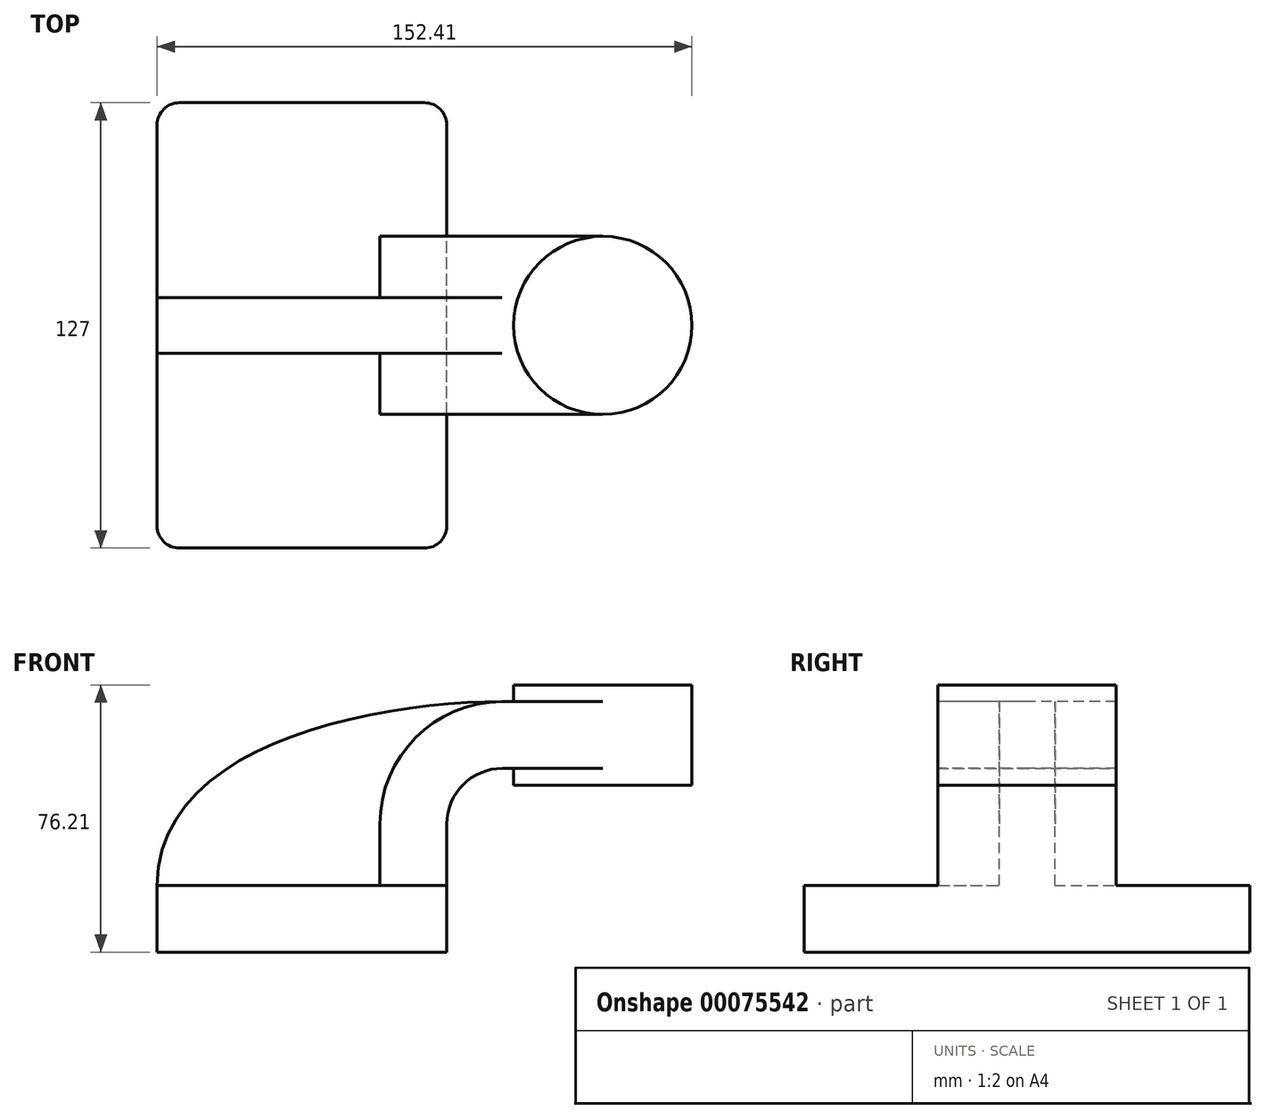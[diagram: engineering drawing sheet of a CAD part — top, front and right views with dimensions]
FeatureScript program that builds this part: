
annotation { "Feature Type Name" : "Feature", "Feature Type Description" : "" }
export const myFeature = defineFeature(function(context is Context, id is Id, definition is map)
    precondition{}
    {
        {
            var Q0;
            Q0=qCreatedBy(makeId("Front.planeOp"),FACE);
            var sketch = newSketch(context, id + "F0", { "sketchPlane" : qUnion([Q0])});
            skLineSegment(sketch, "E0.rect.bottom", {"start": v(-41.28, 9.53) * mm, "end": v(41.27, 9.53) * mm});
            skLineSegment(sketch, "E0.rect.top", {"start": v(-41.28, -9.53) * mm, "end": v(41.27, -9.53) * mm});
            skLineSegment(sketch, "E0.rect.left", {"start": v(-41.28, 9.53) * mm, "end": v(-41.28, -9.53) * mm});
            skLineSegment(sketch, "E0.rect.right", {"start": v(41.27, 9.53) * mm, "end": v(41.27, -9.53) * mm});
            skPoint(sketch, "E0.rect.middle", {"position": v(0, 0) * mm});
            skLineSegment(sketch, "E1.rect.bottom", {"start": v(60.32, 66.67) * mm, "end": v(111.12, 66.67) * mm});
            skLineSegment(sketch, "E1.rect.top", {"start": v(60.32, 38.1) * mm, "end": v(111.12, 38.1) * mm});
            skLineSegment(sketch, "E1.rect.left", {"start": v(60.32, 66.67) * mm, "end": v(60.32, 38.1) * mm});
            skLineSegment(sketch, "E1.rect.right", {"start": v(111.12, 66.67) * mm, "end": v(111.12, 38.1) * mm});
            skPoint(sketch, "E1.rect.middle", {"position": v(85.72, 52.39) * mm});
            skLineSegment(sketch, "E2", {"start": v(41.27, 9.53) * mm, "end": v(41.27, 27) * mm});
            skArc(sketch, "E3", {"start": v(41.27, 27) * mm, "mid": v(45.92, 38.23) * mm, "end": v(57.15, 42.88) * mm});
            skLineSegment(sketch, "E4", {"start": v(57.15, 42.88) * mm, "end": v(85.72, 42.88) * mm});
            skLineSegment(sketch, "E5.0", {"start": v(57.15, 61.93) * mm, "end": v(85.72, 61.93) * mm});
            skArc(sketch, "E5.1", {"start": v(22.22, 27) * mm, "mid": v(32.45, 51.7) * mm, "end": v(57.15, 61.93) * mm});
            skLineSegment(sketch, "E5.2", {"start": v(22.22, 9.53) * mm, "end": v(22.22, 27) * mm});
            skFitSpline(sketch, "E6", {"points": [v(-41.28, 9.52) * mm, v(57.15, 61.93) * mm], "startDerivative": vector(0.52, 122.26) * mm, "endDerivative": vector(107.68, 0.26) * mm});
            skLineSegment(sketch, "E7", {"start": v(85.72, 42.88) * mm, "end": v(85.72, 66.67) * mm});
            skLineSegment(sketch, "E8", {"start": v(85.72, 42.88) * mm, "end": v(85.72, 38.1) * mm});
            skSolve(sketch);
        }
        {
            var Q0;
            Q0=makeQuery(id+"F0.imprint","IMPRINT",FACE,{"disambiguationData":[TD([[makeQuery(id+"F0.imprint","IMPRINT",EDGE,{"derivedFrom":sQuery(id+"F0.wireOp",EDGE,"E0.rect.top")}),1.0]])]});
            extrude(context, id + "F1", {"entities" : qUnion([Q0]), "endBound" : BoundingType.SYMMETRIC, "depth" : 127 * mm});
        }
        {
            var Q0;
            {var subQ6=sQuery(id+"F0.wireOp",EDGE,"E2");Q0=makeQuery(id+"F0.imprint","IMPRINT",FACE,{"disambiguationData":[TD([[makeQuery(id+"F0.imprint","IMPRINT",EDGE,{"derivedFrom":subQ6}),1.0]])]});}
            var Q1;
            {var subQ0=sQuery(id+"F0.wireOp",EDGE,"E5.0");var subQ1=sQuery(id+"F0.wireOp",EDGE,"E1.rect.left");var subQ2=makeQuery(id+"F0.imprint","INTERSECT",VERTEX,{"derivedFrom":[subQ1,subQ0]});Q1=makeQuery(id+"F0.imprint","IMPRINT",FACE,{"disambiguationData":[TD([[makeQuery(id+"F0.imprint","IMPRINT",EDGE,{"disambiguationData":[TD([[subQ2,-1.0]])],"derivedFrom":subQ1}),1.0]])]});}
            extrude(context, id + "F2", {"entities" : qUnion([Q0, Q1]), "operationType" : NewBodyOperationType.ADD, "endBound" : BoundingType.SYMMETRIC, "depth" : 50.8 * mm});
        }
        {
            var Q0;
            {var subQ3=sQuery(id+"F0.wireOp",EDGE,"E5.2");Q0=makeQuery(id+"F0.imprint","IMPRINT",FACE,{"disambiguationData":[TD([[makeQuery(id+"F0.imprint","IMPRINT",EDGE,{"derivedFrom":subQ3}),1.0]])]});}
            extrude(context, id + "F3", {"entities" : qUnion([Q0]), "operationType" : NewBodyOperationType.ADD, "endBound" : BoundingType.SYMMETRIC, "depth" : 15.88 * mm});
        }
        {
            var Q0;
            {var subQ0=sQuery(id+"F0.wireOp",EDGE,"E1.rect.right");Q0=makeQuery(id+"F0.imprint","IMPRINT",FACE,{"disambiguationData":[TD([[makeQuery(id+"F0.imprint","IMPRINT",EDGE,{"derivedFrom":subQ0}),-1.0]])]});}
            var Q1;
            Q1=sQuery(id+"F0.wireOp",EDGE,"E7");
            revolve(context, id + "F4", {"operationType" : NewBodyOperationType.ADD, "entities" : qUnion([Q0]), "axis" : qUnion([Q1]), "revolveType" : RevolveType.FULL});
        }
        {
            var Q0;
            Q0=makeQuery(id+"F1.opExtrude","CAP_EDGE",EDGE,{"disambiguationData":[OSD([sQuery(id+"F0.wireOp",EDGE,"E0.rect.right")])],"isStart":false});
            var Q1;
            Q1=makeQuery(id+"F1.opExtrude","CAP_EDGE",EDGE,{"disambiguationData":[OSD([sQuery(id+"F0.wireOp",EDGE,"E0.rect.left")])],"isStart":false});
            var Q2;
            Q2=makeQuery(id+"F1.opExtrude","CAP_EDGE",EDGE,{"disambiguationData":[OSD([sQuery(id+"F0.wireOp",EDGE,"E0.rect.left")])],"isStart":true});
            var Q3;
            Q3=makeQuery(id+"F1.opExtrude","CAP_EDGE",EDGE,{"disambiguationData":[OSD([sQuery(id+"F0.wireOp",EDGE,"E0.rect.right")])],"isStart":true});
            fillet(context, id + "F5", {"entities" : qUnion([Q0, Q1, Q2, Q3]), "radius" : 6.35 * mm, "tangentPropagation" : true, "allowEdgeOverflow" : false});
        }
    });
